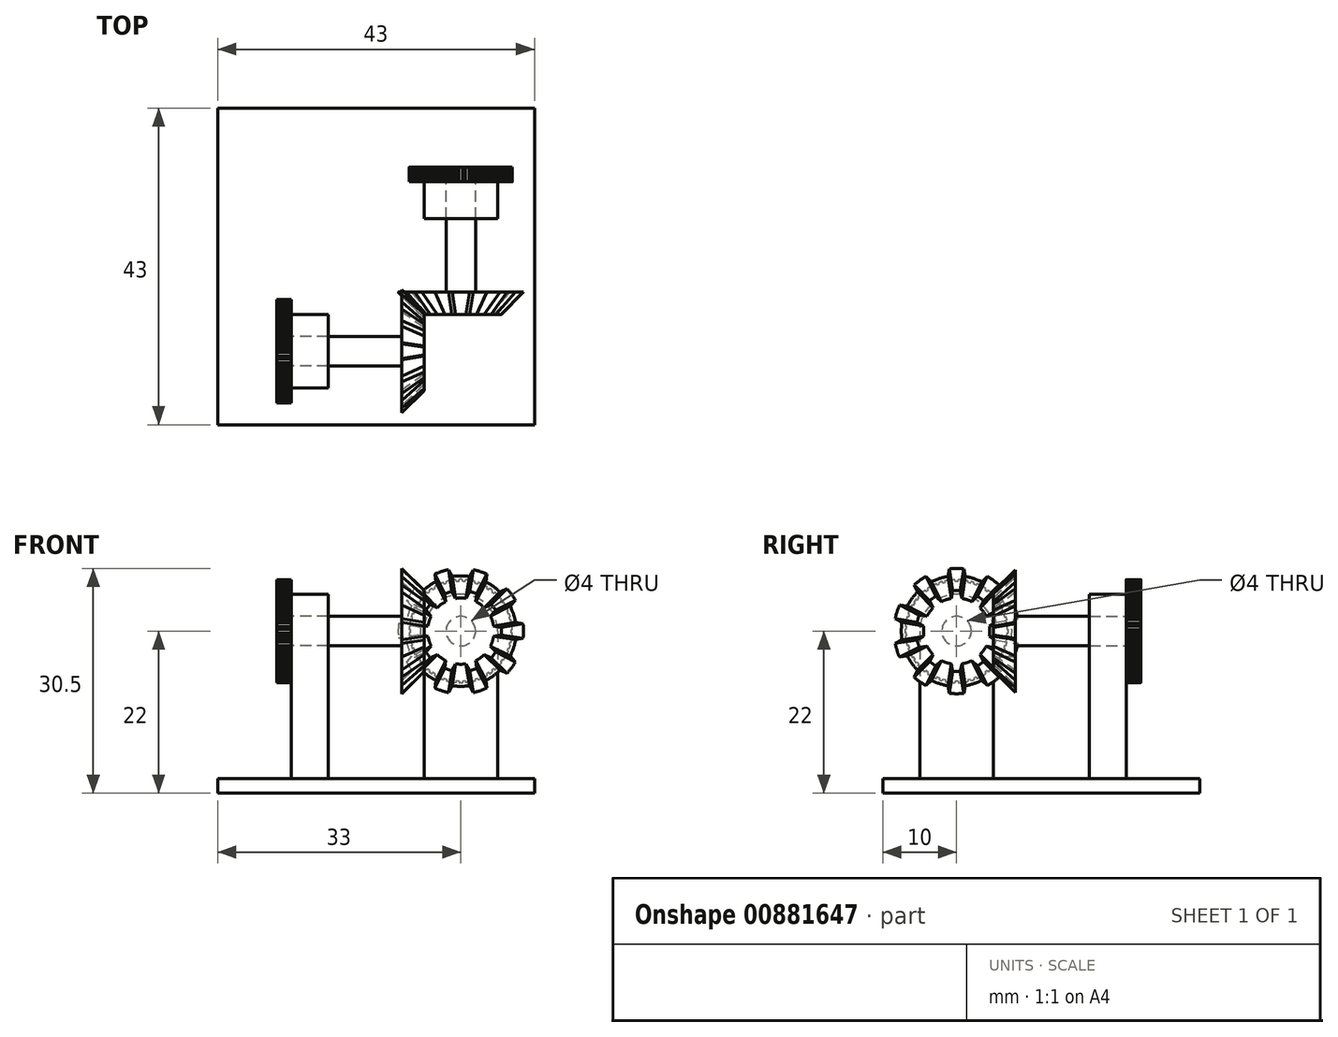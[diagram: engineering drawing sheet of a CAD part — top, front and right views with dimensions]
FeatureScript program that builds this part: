
annotation { "Feature Type Name" : "Feature", "Feature Type Description" : "" }
export const myFeature = defineFeature(function(context is Context, id is Id, definition is map)
    precondition{}
    {
        {
            var Q0;
            Q0=qCreatedBy(makeId("Top.planeOp"),FACE);
            var sketch = newSketch(context, id + "F0", { "sketchPlane" : qUnion([Q0])});
            skLineSegment(sketch, "E0", {"start": v(5, -5) * mm, "end": v(8, -8) * mm, "construction": true});
            skLineSegment(sketch, "E1", {"start": v(8, -8) * mm, "end": v(8, -2) * mm});
            skLineSegment(sketch, "E2", {"start": v(8, -2) * mm, "end": v(23, -2) * mm});
            skLineSegment(sketch, "E3", {"start": v(23, -2) * mm, "end": v(23, -7) * mm});
            skLineSegment(sketch, "E4", {"start": v(23, -7) * mm, "end": v(25, -7) * mm});
            skLineSegment(sketch, "E5", {"start": v(25, -7) * mm, "end": v(25, 0) * mm});
            skLineSegment(sketch, "E6", {"start": v(25, 0) * mm, "end": v(5, 0) * mm});
            skLineSegment(sketch, "E7", {"start": v(5, -5) * mm, "end": v(5, 0) * mm});
            skLineSegment(sketch, "E8", {"start": v(5, -5) * mm, "end": v(5, -5.5) * mm});
            skLineSegment(sketch, "E9", {"start": v(5, -5.5) * mm, "end": v(8, -8.5) * mm});
            skLineSegment(sketch, "E10", {"start": v(8, -8.5) * mm, "end": v(8, -8) * mm});
            skSolve(sketch);
        }
        {
            var Q0;
            Q0=makeQuery(id+"F0.imprint","IMPRINT",FACE,{"disambiguationData":[TD([[makeQuery(id+"F0.imprint","IMPRINT",EDGE,{"derivedFrom":sQuery(id+"F0.wireOp",EDGE,"E1")}),1.0]])]});
            var Q1;
            Q1=sQuery(id+"F0.wireOp",EDGE,"E6");
            revolve(context, id + "F1", {"surfaceOperationType" : NewSurfaceOperationType.NEW, "entities" : qUnion([Q0]), "axis" : qUnion([Q1]), "revolveType" : RevolveType.FULL});
        }
        {
            var Q0;
            Q0=makeQuery(id+"F1.opRevolve","SWEPT_FACE",FACE,{"disambiguationData":[OSD([sQuery(id+"F0.wireOp",EDGE,"E5")])]});
            var sketch = newSketch(context, id + "F2", { "sketchPlane" : qUnion([Q0])});
            skLineSegment(sketch, "E11", {"start": v(0.2, 7) * mm, "end": v(0.2, 6.8) * mm});
            skLineSegment(sketch, "E12", {"start": v(0.2, 6.8) * mm, "end": v(0, 6.8) * mm});
            skLineSegment(sketch, "E13.MirrorCS", {"start": v(-0.2, 6.8) * mm, "end": v(0, 6.8) * mm});
            skLineSegment(sketch, "E14.MirrorCS", {"start": v(-0.2, 7) * mm, "end": v(-0.2, 6.8) * mm});
            skArc(sketch, "E15", {"start": v(-0.2, 7) * mm, "mid": v(0, 7) * mm, "end": v(0.2, 7) * mm});
            skLineSegment(sketch, "E16.1.0", {"start": v(-1.08, 6.92) * mm, "end": v(-1.05, 6.72) * mm});
            skArc(sketch, "E16.1.1", {"start": v(-1.08, 6.92) * mm, "mid": v(-0.88, 6.94) * mm, "end": v(-0.68, 6.97) * mm});
            skLineSegment(sketch, "E16.1.2", {"start": v(-0.68, 6.97) * mm, "end": v(-0.65, 6.77) * mm});
            skLineSegment(sketch, "E16.1.3", {"start": v(-0.65, 6.77) * mm, "end": v(-0.85, 6.74) * mm});
            skLineSegment(sketch, "E16.1.4", {"start": v(-1.05, 6.72) * mm, "end": v(-0.85, 6.74) * mm});
            skLineSegment(sketch, "E16.2.0", {"start": v(-1.93, 6.73) * mm, "end": v(-1.88, 6.53) * mm});
            skArc(sketch, "E16.2.1", {"start": v(-1.93, 6.73) * mm, "mid": v(-1.74, 6.78) * mm, "end": v(-1.55, 6.83) * mm});
            skLineSegment(sketch, "E16.2.2", {"start": v(-1.55, 6.83) * mm, "end": v(-1.5, 6.63) * mm});
            skLineSegment(sketch, "E16.2.3", {"start": v(-1.5, 6.63) * mm, "end": v(-1.7, 6.58) * mm});
            skLineSegment(sketch, "E16.2.4", {"start": v(-1.88, 6.53) * mm, "end": v(-1.7, 6.58) * mm});
            skLineSegment(sketch, "E17.2.3.0", {"start": v(-2.76, 6.43) * mm, "end": v(-2.69, 6.25) * mm});
            skArc(sketch, "E17.3.3.0", {"start": v(-2.76, 6.43) * mm, "mid": v(-2.58, 6.5) * mm, "end": v(-2.39, 6.58) * mm});
            skLineSegment(sketch, "E17.7.3.0", {"start": v(-2.39, 6.58) * mm, "end": v(-2.32, 6.4) * mm});
            skLineSegment(sketch, "E17.10.3.0", {"start": v(-2.32, 6.4) * mm, "end": v(-2.5, 6.32) * mm});
            skLineSegment(sketch, "E17.13.3.0", {"start": v(-2.69, 6.25) * mm, "end": v(-2.5, 6.32) * mm});
            skLineSegment(sketch, "E17.2.4.0", {"start": v(-3.55, 6.04) * mm, "end": v(-3.45, 5.86) * mm});
            skArc(sketch, "E17.3.4.0", {"start": v(-3.55, 6.04) * mm, "mid": v(-3.37, 6.13) * mm, "end": v(-3.2, 6.23) * mm});
            skLineSegment(sketch, "E17.7.4.0", {"start": v(-3.2, 6.23) * mm, "end": v(-3.1, 6.05) * mm});
            skLineSegment(sketch, "E17.10.4.0", {"start": v(-3.1, 6.05) * mm, "end": v(-3.27, 5.96) * mm});
            skLineSegment(sketch, "E17.13.4.0", {"start": v(-3.45, 5.86) * mm, "end": v(-3.27, 5.96) * mm});
            skLineSegment(sketch, "E17.2.5.0", {"start": v(-4.27, 5.54) * mm, "end": v(-4.16, 5.38) * mm});
            skArc(sketch, "E17.3.5.0", {"start": v(-4.27, 5.54) * mm, "mid": v(-4.11, 5.66) * mm, "end": v(-3.95, 5.78) * mm});
            skLineSegment(sketch, "E17.7.5.0", {"start": v(-3.95, 5.78) * mm, "end": v(-3.83, 5.62) * mm});
            skLineSegment(sketch, "E17.10.5.0", {"start": v(-3.83, 5.62) * mm, "end": v(-4, 5.5) * mm});
            skLineSegment(sketch, "E17.13.5.0", {"start": v(-4.16, 5.38) * mm, "end": v(-4, 5.5) * mm});
            skLineSegment(sketch, "E17.2.6.0", {"start": v(-4.94, 4.96) * mm, "end": v(-4.8, 4.82) * mm});
            skArc(sketch, "E17.3.6.0", {"start": v(-4.94, 4.96) * mm, "mid": v(-4.8, 5.1) * mm, "end": v(-4.64, 5.24) * mm});
            skLineSegment(sketch, "E17.7.6.0", {"start": v(-4.64, 5.24) * mm, "end": v(-4.5, 5.1) * mm});
            skLineSegment(sketch, "E17.10.6.0", {"start": v(-4.5, 5.1) * mm, "end": v(-4.65, 4.95) * mm});
            skLineSegment(sketch, "E17.13.6.0", {"start": v(-4.8, 4.82) * mm, "end": v(-4.65, 4.95) * mm});
            skLineSegment(sketch, "E17.2.7.0", {"start": v(-5.52, 4.3) * mm, "end": v(-5.36, 4.18) * mm});
            skArc(sketch, "E17.3.7.0", {"start": v(-5.52, 4.3) * mm, "mid": v(-5.4, 4.46) * mm, "end": v(-5.26, 4.61) * mm});
            skLineSegment(sketch, "E17.7.7.0", {"start": v(-5.26, 4.61) * mm, "end": v(-5.1, 4.49) * mm});
            skLineSegment(sketch, "E17.10.7.0", {"start": v(-5.1, 4.49) * mm, "end": v(-5.24, 4.33) * mm});
            skLineSegment(sketch, "E17.13.7.0", {"start": v(-5.36, 4.18) * mm, "end": v(-5.24, 4.33) * mm});
            skLineSegment(sketch, "E17.2.8.0", {"start": v(-6.02, 3.58) * mm, "end": v(-5.85, 3.47) * mm});
            skArc(sketch, "E17.3.8.0", {"start": v(-6.02, 3.58) * mm, "mid": v(-5.91, 3.75) * mm, "end": v(-5.8, 3.92) * mm});
            skLineSegment(sketch, "E17.7.8.0", {"start": v(-5.8, 3.92) * mm, "end": v(-5.63, 3.81) * mm});
            skLineSegment(sketch, "E17.10.8.0", {"start": v(-5.63, 3.81) * mm, "end": v(-5.74, 3.64) * mm});
            skLineSegment(sketch, "E17.13.8.0", {"start": v(-5.85, 3.47) * mm, "end": v(-5.74, 3.64) * mm});
            skLineSegment(sketch, "E17.2.9.0", {"start": v(-6.42, 2.8) * mm, "end": v(-6.24, 2.71) * mm});
            skArc(sketch, "E17.3.9.0", {"start": v(-6.42, 2.8) * mm, "mid": v(-6.33, 2.98) * mm, "end": v(-6.25, 3.16) * mm});
            skLineSegment(sketch, "E17.7.9.0", {"start": v(-6.25, 3.16) * mm, "end": v(-6.07, 3.08) * mm});
            skLineSegment(sketch, "E17.10.9.0", {"start": v(-6.07, 3.08) * mm, "end": v(-6.15, 2.9) * mm});
            skLineSegment(sketch, "E17.13.9.0", {"start": v(-6.24, 2.71) * mm, "end": v(-6.15, 2.9) * mm});
            skLineSegment(sketch, "E17.2.10.0", {"start": v(-6.72, 1.97) * mm, "end": v(-6.53, 1.91) * mm});
            skArc(sketch, "E17.3.10.0", {"start": v(-6.72, 1.97) * mm, "mid": v(-6.66, 2.16) * mm, "end": v(-6.6, 2.35) * mm});
            skLineSegment(sketch, "E17.7.10.0", {"start": v(-6.6, 2.35) * mm, "end": v(-6.4, 2.3) * mm});
            skLineSegment(sketch, "E17.10.10.0", {"start": v(-6.4, 2.3) * mm, "end": v(-6.46, 2.1) * mm});
            skLineSegment(sketch, "E17.13.10.0", {"start": v(-6.53, 1.91) * mm, "end": v(-6.46, 2.1) * mm});
            skLineSegment(sketch, "E17.2.11.0", {"start": v(-6.91, 1.11) * mm, "end": v(-6.71, 1.08) * mm});
            skArc(sketch, "E17.3.11.0", {"start": v(-6.91, 1.11) * mm, "mid": v(-6.88, 1.31) * mm, "end": v(-6.84, 1.5) * mm});
            skLineSegment(sketch, "E17.7.11.0", {"start": v(-6.84, 1.5) * mm, "end": v(-6.64, 1.47) * mm});
            skLineSegment(sketch, "E17.10.11.0", {"start": v(-6.64, 1.47) * mm, "end": v(-6.68, 1.27) * mm});
            skLineSegment(sketch, "E17.13.11.0", {"start": v(-6.71, 1.08) * mm, "end": v(-6.68, 1.27) * mm});
            skLineSegment(sketch, "E17.2.12.0", {"start": v(-7, 0.24) * mm, "end": v(-6.8, 0.23) * mm});
            skArc(sketch, "E17.3.12.0", {"start": v(-7, 0.24) * mm, "mid": v(-6.99, 0.44) * mm, "end": v(-6.97, 0.64) * mm});
            skLineSegment(sketch, "E17.7.12.0", {"start": v(-6.97, 0.64) * mm, "end": v(-6.77, 0.63) * mm});
            skLineSegment(sketch, "E17.10.12.0", {"start": v(-6.77, 0.63) * mm, "end": v(-6.78, 0.43) * mm});
            skLineSegment(sketch, "E17.13.12.0", {"start": v(-6.8, 0.23) * mm, "end": v(-6.78, 0.43) * mm});
            skLineSegment(sketch, "E17.2.13.0", {"start": v(-6.97, -0.64) * mm, "end": v(-6.77, -0.63) * mm});
            skArc(sketch, "E17.3.13.0", {"start": v(-6.97, -0.64) * mm, "mid": v(-6.99, -0.44) * mm, "end": v(-7, -0.24) * mm});
            skLineSegment(sketch, "E17.7.13.0", {"start": v(-7, -0.24) * mm, "end": v(-6.8, -0.23) * mm});
            skLineSegment(sketch, "E17.10.13.0", {"start": v(-6.8, -0.23) * mm, "end": v(-6.78, -0.43) * mm});
            skLineSegment(sketch, "E17.13.13.0", {"start": v(-6.77, -0.63) * mm, "end": v(-6.78, -0.43) * mm});
            skLineSegment(sketch, "E17.2.14.0", {"start": v(-6.84, -1.5) * mm, "end": v(-6.64, -1.47) * mm});
            skArc(sketch, "E17.3.14.0", {"start": v(-6.84, -1.5) * mm, "mid": v(-6.88, -1.31) * mm, "end": v(-6.91, -1.11) * mm});
            skLineSegment(sketch, "E17.7.14.0", {"start": v(-6.91, -1.11) * mm, "end": v(-6.71, -1.08) * mm});
            skLineSegment(sketch, "E17.10.14.0", {"start": v(-6.71, -1.08) * mm, "end": v(-6.68, -1.27) * mm});
            skLineSegment(sketch, "E17.13.14.0", {"start": v(-6.64, -1.47) * mm, "end": v(-6.68, -1.27) * mm});
            skLineSegment(sketch, "E17.2.15.0", {"start": v(-6.6, -2.35) * mm, "end": v(-6.4, -2.3) * mm});
            skArc(sketch, "E17.3.15.0", {"start": v(-6.6, -2.35) * mm, "mid": v(-6.66, -2.16) * mm, "end": v(-6.72, -1.97) * mm});
            skLineSegment(sketch, "E17.7.15.0", {"start": v(-6.72, -1.97) * mm, "end": v(-6.53, -1.91) * mm});
            skLineSegment(sketch, "E17.10.15.0", {"start": v(-6.53, -1.91) * mm, "end": v(-6.46, -2.1) * mm});
            skLineSegment(sketch, "E17.13.15.0", {"start": v(-6.4, -2.3) * mm, "end": v(-6.46, -2.1) * mm});
            skLineSegment(sketch, "E17.2.16.0", {"start": v(-6.25, -3.16) * mm, "end": v(-6.07, -3.08) * mm});
            skArc(sketch, "E17.3.16.0", {"start": v(-6.25, -3.16) * mm, "mid": v(-6.33, -2.98) * mm, "end": v(-6.42, -2.8) * mm});
            skLineSegment(sketch, "E17.7.16.0", {"start": v(-6.42, -2.8) * mm, "end": v(-6.24, -2.71) * mm});
            skLineSegment(sketch, "E17.10.16.0", {"start": v(-6.24, -2.71) * mm, "end": v(-6.15, -2.9) * mm});
            skLineSegment(sketch, "E17.13.16.0", {"start": v(-6.07, -3.08) * mm, "end": v(-6.15, -2.9) * mm});
            skLineSegment(sketch, "E17.2.17.0", {"start": v(-5.8, -3.92) * mm, "end": v(-5.63, -3.81) * mm});
            skArc(sketch, "E17.3.17.0", {"start": v(-5.8, -3.92) * mm, "mid": v(-5.91, -3.75) * mm, "end": v(-6.02, -3.58) * mm});
            skLineSegment(sketch, "E17.7.17.0", {"start": v(-6.02, -3.58) * mm, "end": v(-5.85, -3.47) * mm});
            skLineSegment(sketch, "E17.10.17.0", {"start": v(-5.85, -3.47) * mm, "end": v(-5.74, -3.64) * mm});
            skLineSegment(sketch, "E17.13.17.0", {"start": v(-5.63, -3.81) * mm, "end": v(-5.74, -3.64) * mm});
            skLineSegment(sketch, "E17.2.18.0", {"start": v(-5.26, -4.61) * mm, "end": v(-5.1, -4.49) * mm});
            skArc(sketch, "E17.3.18.0", {"start": v(-5.26, -4.61) * mm, "mid": v(-5.4, -4.46) * mm, "end": v(-5.52, -4.3) * mm});
            skLineSegment(sketch, "E17.7.18.0", {"start": v(-5.52, -4.3) * mm, "end": v(-5.36, -4.18) * mm});
            skLineSegment(sketch, "E17.10.18.0", {"start": v(-5.36, -4.18) * mm, "end": v(-5.24, -4.33) * mm});
            skLineSegment(sketch, "E17.13.18.0", {"start": v(-5.1, -4.49) * mm, "end": v(-5.24, -4.33) * mm});
            skLineSegment(sketch, "E17.2.19.0", {"start": v(-4.64, -5.24) * mm, "end": v(-4.5, -5.1) * mm});
            skArc(sketch, "E17.3.19.0", {"start": v(-4.64, -5.24) * mm, "mid": v(-4.8, -5.1) * mm, "end": v(-4.94, -4.96) * mm});
            skLineSegment(sketch, "E17.7.19.0", {"start": v(-4.94, -4.96) * mm, "end": v(-4.8, -4.82) * mm});
            skLineSegment(sketch, "E17.10.19.0", {"start": v(-4.8, -4.82) * mm, "end": v(-4.65, -4.95) * mm});
            skLineSegment(sketch, "E17.13.19.0", {"start": v(-4.5, -5.1) * mm, "end": v(-4.65, -4.95) * mm});
            skLineSegment(sketch, "E17.2.20.0", {"start": v(-3.95, -5.78) * mm, "end": v(-3.83, -5.62) * mm});
            skArc(sketch, "E17.3.20.0", {"start": v(-3.95, -5.78) * mm, "mid": v(-4.11, -5.66) * mm, "end": v(-4.27, -5.54) * mm});
            skLineSegment(sketch, "E17.7.20.0", {"start": v(-4.27, -5.54) * mm, "end": v(-4.16, -5.38) * mm});
            skLineSegment(sketch, "E17.10.20.0", {"start": v(-4.16, -5.38) * mm, "end": v(-4, -5.5) * mm});
            skLineSegment(sketch, "E17.13.20.0", {"start": v(-3.83, -5.62) * mm, "end": v(-4, -5.5) * mm});
            skLineSegment(sketch, "E17.2.21.0", {"start": v(-3.2, -6.23) * mm, "end": v(-3.1, -6.05) * mm});
            skArc(sketch, "E17.3.21.0", {"start": v(-3.2, -6.23) * mm, "mid": v(-3.37, -6.13) * mm, "end": v(-3.55, -6.04) * mm});
            skLineSegment(sketch, "E17.7.21.0", {"start": v(-3.55, -6.04) * mm, "end": v(-3.45, -5.86) * mm});
            skLineSegment(sketch, "E17.10.21.0", {"start": v(-3.45, -5.86) * mm, "end": v(-3.27, -5.96) * mm});
            skLineSegment(sketch, "E17.13.21.0", {"start": v(-3.1, -6.05) * mm, "end": v(-3.27, -5.96) * mm});
            skLineSegment(sketch, "E17.2.22.0", {"start": v(-2.39, -6.58) * mm, "end": v(-2.32, -6.4) * mm});
            skArc(sketch, "E17.3.22.0", {"start": v(-2.39, -6.58) * mm, "mid": v(-2.58, -6.5) * mm, "end": v(-2.76, -6.43) * mm});
            skLineSegment(sketch, "E17.7.22.0", {"start": v(-2.76, -6.43) * mm, "end": v(-2.69, -6.25) * mm});
            skLineSegment(sketch, "E17.10.22.0", {"start": v(-2.69, -6.25) * mm, "end": v(-2.5, -6.32) * mm});
            skLineSegment(sketch, "E17.13.22.0", {"start": v(-2.32, -6.4) * mm, "end": v(-2.5, -6.32) * mm});
            skLineSegment(sketch, "E17.2.23.0", {"start": v(-1.55, -6.83) * mm, "end": v(-1.5, -6.63) * mm});
            skArc(sketch, "E17.3.23.0", {"start": v(-1.55, -6.83) * mm, "mid": v(-1.74, -6.78) * mm, "end": v(-1.93, -6.73) * mm});
            skLineSegment(sketch, "E17.7.23.0", {"start": v(-1.93, -6.73) * mm, "end": v(-1.88, -6.53) * mm});
            skLineSegment(sketch, "E17.10.23.0", {"start": v(-1.88, -6.53) * mm, "end": v(-1.7, -6.58) * mm});
            skLineSegment(sketch, "E17.13.23.0", {"start": v(-1.5, -6.63) * mm, "end": v(-1.7, -6.58) * mm});
            skLineSegment(sketch, "E17.2.24.0", {"start": v(-0.68, -6.97) * mm, "end": v(-0.65, -6.77) * mm});
            skArc(sketch, "E17.3.24.0", {"start": v(-0.68, -6.97) * mm, "mid": v(-0.88, -6.94) * mm, "end": v(-1.08, -6.92) * mm});
            skLineSegment(sketch, "E17.7.24.0", {"start": v(-1.08, -6.92) * mm, "end": v(-1.05, -6.72) * mm});
            skLineSegment(sketch, "E17.10.24.0", {"start": v(-1.05, -6.72) * mm, "end": v(-0.85, -6.74) * mm});
            skLineSegment(sketch, "E17.13.24.0", {"start": v(-0.65, -6.77) * mm, "end": v(-0.85, -6.74) * mm});
            skLineSegment(sketch, "E17.2.25.0", {"start": v(0.2, -7) * mm, "end": v(0.2, -6.8) * mm});
            skArc(sketch, "E17.3.25.0", {"start": v(0.2, -7) * mm, "mid": v(0, -7) * mm, "end": v(-0.2, -7) * mm});
            skLineSegment(sketch, "E17.7.25.0", {"start": v(-0.2, -7) * mm, "end": v(-0.2, -6.8) * mm});
            skLineSegment(sketch, "E17.10.25.0", {"start": v(-0.2, -6.8) * mm, "end": v(0, -6.8) * mm});
            skLineSegment(sketch, "E17.13.25.0", {"start": v(0.2, -6.8) * mm, "end": v(0, -6.8) * mm});
            skLineSegment(sketch, "E17.2.26.0", {"start": v(1.08, -6.92) * mm, "end": v(1.05, -6.72) * mm});
            skArc(sketch, "E17.3.26.0", {"start": v(1.08, -6.92) * mm, "mid": v(0.88, -6.94) * mm, "end": v(0.68, -6.97) * mm});
            skLineSegment(sketch, "E17.7.26.0", {"start": v(0.68, -6.97) * mm, "end": v(0.65, -6.77) * mm});
            skLineSegment(sketch, "E17.10.26.0", {"start": v(0.65, -6.77) * mm, "end": v(0.85, -6.74) * mm});
            skLineSegment(sketch, "E17.13.26.0", {"start": v(1.05, -6.72) * mm, "end": v(0.85, -6.74) * mm});
            skLineSegment(sketch, "E17.2.27.0", {"start": v(1.93, -6.73) * mm, "end": v(1.88, -6.53) * mm});
            skArc(sketch, "E17.3.27.0", {"start": v(1.93, -6.73) * mm, "mid": v(1.74, -6.78) * mm, "end": v(1.55, -6.83) * mm});
            skLineSegment(sketch, "E17.7.27.0", {"start": v(1.55, -6.83) * mm, "end": v(1.5, -6.63) * mm});
            skLineSegment(sketch, "E17.10.27.0", {"start": v(1.5, -6.63) * mm, "end": v(1.7, -6.58) * mm});
            skLineSegment(sketch, "E17.13.27.0", {"start": v(1.88, -6.53) * mm, "end": v(1.7, -6.58) * mm});
            skLineSegment(sketch, "E17.2.28.0", {"start": v(2.76, -6.43) * mm, "end": v(2.69, -6.25) * mm});
            skArc(sketch, "E17.3.28.0", {"start": v(2.76, -6.43) * mm, "mid": v(2.58, -6.5) * mm, "end": v(2.39, -6.58) * mm});
            skLineSegment(sketch, "E17.7.28.0", {"start": v(2.39, -6.58) * mm, "end": v(2.32, -6.4) * mm});
            skLineSegment(sketch, "E17.10.28.0", {"start": v(2.32, -6.4) * mm, "end": v(2.5, -6.32) * mm});
            skLineSegment(sketch, "E17.13.28.0", {"start": v(2.69, -6.25) * mm, "end": v(2.5, -6.32) * mm});
            skLineSegment(sketch, "E17.2.29.0", {"start": v(3.55, -6.04) * mm, "end": v(3.45, -5.86) * mm});
            skArc(sketch, "E17.3.29.0", {"start": v(3.55, -6.04) * mm, "mid": v(3.37, -6.13) * mm, "end": v(3.2, -6.23) * mm});
            skLineSegment(sketch, "E17.7.29.0", {"start": v(3.2, -6.23) * mm, "end": v(3.1, -6.05) * mm});
            skLineSegment(sketch, "E17.10.29.0", {"start": v(3.1, -6.05) * mm, "end": v(3.27, -5.96) * mm});
            skLineSegment(sketch, "E17.13.29.0", {"start": v(3.45, -5.86) * mm, "end": v(3.27, -5.96) * mm});
            skLineSegment(sketch, "E17.2.30.0", {"start": v(4.27, -5.54) * mm, "end": v(4.16, -5.38) * mm});
            skArc(sketch, "E17.3.30.0", {"start": v(4.27, -5.54) * mm, "mid": v(4.11, -5.66) * mm, "end": v(3.95, -5.78) * mm});
            skLineSegment(sketch, "E17.7.30.0", {"start": v(3.95, -5.78) * mm, "end": v(3.83, -5.62) * mm});
            skLineSegment(sketch, "E17.10.30.0", {"start": v(3.83, -5.62) * mm, "end": v(4, -5.5) * mm});
            skLineSegment(sketch, "E17.13.30.0", {"start": v(4.16, -5.38) * mm, "end": v(4, -5.5) * mm});
            skLineSegment(sketch, "E17.2.31.0", {"start": v(4.94, -4.96) * mm, "end": v(4.8, -4.82) * mm});
            skArc(sketch, "E17.3.31.0", {"start": v(4.94, -4.96) * mm, "mid": v(4.8, -5.1) * mm, "end": v(4.64, -5.24) * mm});
            skLineSegment(sketch, "E17.7.31.0", {"start": v(4.64, -5.24) * mm, "end": v(4.5, -5.1) * mm});
            skLineSegment(sketch, "E17.10.31.0", {"start": v(4.5, -5.1) * mm, "end": v(4.65, -4.95) * mm});
            skLineSegment(sketch, "E17.13.31.0", {"start": v(4.8, -4.82) * mm, "end": v(4.65, -4.95) * mm});
            skLineSegment(sketch, "E17.2.32.0", {"start": v(5.52, -4.3) * mm, "end": v(5.36, -4.18) * mm});
            skArc(sketch, "E17.3.32.0", {"start": v(5.52, -4.3) * mm, "mid": v(5.4, -4.46) * mm, "end": v(5.26, -4.61) * mm});
            skLineSegment(sketch, "E17.7.32.0", {"start": v(5.26, -4.61) * mm, "end": v(5.1, -4.49) * mm});
            skLineSegment(sketch, "E17.10.32.0", {"start": v(5.1, -4.49) * mm, "end": v(5.24, -4.33) * mm});
            skLineSegment(sketch, "E17.13.32.0", {"start": v(5.36, -4.18) * mm, "end": v(5.24, -4.33) * mm});
            skLineSegment(sketch, "E17.2.33.0", {"start": v(6.02, -3.58) * mm, "end": v(5.85, -3.47) * mm});
            skArc(sketch, "E17.3.33.0", {"start": v(6.02, -3.58) * mm, "mid": v(5.91, -3.75) * mm, "end": v(5.8, -3.92) * mm});
            skLineSegment(sketch, "E17.7.33.0", {"start": v(5.8, -3.92) * mm, "end": v(5.63, -3.81) * mm});
            skLineSegment(sketch, "E17.10.33.0", {"start": v(5.63, -3.81) * mm, "end": v(5.74, -3.64) * mm});
            skLineSegment(sketch, "E17.13.33.0", {"start": v(5.85, -3.47) * mm, "end": v(5.74, -3.64) * mm});
            skLineSegment(sketch, "E17.2.34.0", {"start": v(6.42, -2.8) * mm, "end": v(6.24, -2.71) * mm});
            skArc(sketch, "E17.3.34.0", {"start": v(6.42, -2.8) * mm, "mid": v(6.33, -2.98) * mm, "end": v(6.25, -3.16) * mm});
            skLineSegment(sketch, "E17.7.34.0", {"start": v(6.25, -3.16) * mm, "end": v(6.07, -3.08) * mm});
            skLineSegment(sketch, "E17.10.34.0", {"start": v(6.07, -3.08) * mm, "end": v(6.15, -2.9) * mm});
            skLineSegment(sketch, "E17.13.34.0", {"start": v(6.24, -2.71) * mm, "end": v(6.15, -2.9) * mm});
            skLineSegment(sketch, "E17.2.35.0", {"start": v(6.72, -1.97) * mm, "end": v(6.53, -1.91) * mm});
            skArc(sketch, "E17.3.35.0", {"start": v(6.72, -1.97) * mm, "mid": v(6.66, -2.16) * mm, "end": v(6.6, -2.35) * mm});
            skLineSegment(sketch, "E17.7.35.0", {"start": v(6.6, -2.35) * mm, "end": v(6.4, -2.3) * mm});
            skLineSegment(sketch, "E17.10.35.0", {"start": v(6.4, -2.3) * mm, "end": v(6.46, -2.1) * mm});
            skLineSegment(sketch, "E17.13.35.0", {"start": v(6.53, -1.91) * mm, "end": v(6.46, -2.1) * mm});
            skLineSegment(sketch, "E17.2.36.0", {"start": v(6.91, -1.11) * mm, "end": v(6.71, -1.08) * mm});
            skArc(sketch, "E17.3.36.0", {"start": v(6.91, -1.11) * mm, "mid": v(6.88, -1.31) * mm, "end": v(6.84, -1.5) * mm});
            skLineSegment(sketch, "E17.7.36.0", {"start": v(6.84, -1.5) * mm, "end": v(6.64, -1.47) * mm});
            skLineSegment(sketch, "E17.10.36.0", {"start": v(6.64, -1.47) * mm, "end": v(6.68, -1.27) * mm});
            skLineSegment(sketch, "E17.13.36.0", {"start": v(6.71, -1.08) * mm, "end": v(6.68, -1.27) * mm});
            skLineSegment(sketch, "E17.2.37.0", {"start": v(7, -0.24) * mm, "end": v(6.8, -0.23) * mm});
            skArc(sketch, "E17.3.37.0", {"start": v(7, -0.24) * mm, "mid": v(6.99, -0.44) * mm, "end": v(6.97, -0.64) * mm});
            skLineSegment(sketch, "E17.7.37.0", {"start": v(6.97, -0.64) * mm, "end": v(6.77, -0.63) * mm});
            skLineSegment(sketch, "E17.10.37.0", {"start": v(6.77, -0.63) * mm, "end": v(6.78, -0.43) * mm});
            skLineSegment(sketch, "E17.13.37.0", {"start": v(6.8, -0.23) * mm, "end": v(6.78, -0.43) * mm});
            skLineSegment(sketch, "E17.2.38.0", {"start": v(6.97, 0.64) * mm, "end": v(6.77, 0.63) * mm});
            skArc(sketch, "E17.3.38.0", {"start": v(6.97, 0.64) * mm, "mid": v(6.99, 0.44) * mm, "end": v(7, 0.24) * mm});
            skLineSegment(sketch, "E17.7.38.0", {"start": v(7, 0.24) * mm, "end": v(6.8, 0.23) * mm});
            skLineSegment(sketch, "E17.10.38.0", {"start": v(6.8, 0.23) * mm, "end": v(6.78, 0.43) * mm});
            skLineSegment(sketch, "E17.13.38.0", {"start": v(6.77, 0.63) * mm, "end": v(6.78, 0.43) * mm});
            skLineSegment(sketch, "E17.2.39.0", {"start": v(6.84, 1.5) * mm, "end": v(6.64, 1.47) * mm});
            skArc(sketch, "E17.3.39.0", {"start": v(6.84, 1.5) * mm, "mid": v(6.88, 1.31) * mm, "end": v(6.91, 1.11) * mm});
            skLineSegment(sketch, "E17.7.39.0", {"start": v(6.91, 1.11) * mm, "end": v(6.71, 1.08) * mm});
            skLineSegment(sketch, "E17.10.39.0", {"start": v(6.71, 1.08) * mm, "end": v(6.68, 1.27) * mm});
            skLineSegment(sketch, "E17.13.39.0", {"start": v(6.64, 1.47) * mm, "end": v(6.68, 1.27) * mm});
            skLineSegment(sketch, "E17.2.40.0", {"start": v(6.6, 2.35) * mm, "end": v(6.4, 2.3) * mm});
            skArc(sketch, "E17.3.40.0", {"start": v(6.6, 2.35) * mm, "mid": v(6.66, 2.16) * mm, "end": v(6.72, 1.97) * mm});
            skLineSegment(sketch, "E17.7.40.0", {"start": v(6.72, 1.97) * mm, "end": v(6.53, 1.91) * mm});
            skLineSegment(sketch, "E17.10.40.0", {"start": v(6.53, 1.91) * mm, "end": v(6.46, 2.1) * mm});
            skLineSegment(sketch, "E17.13.40.0", {"start": v(6.4, 2.3) * mm, "end": v(6.46, 2.1) * mm});
            skLineSegment(sketch, "E17.2.41.0", {"start": v(6.25, 3.16) * mm, "end": v(6.07, 3.08) * mm});
            skArc(sketch, "E17.3.41.0", {"start": v(6.25, 3.16) * mm, "mid": v(6.33, 2.98) * mm, "end": v(6.42, 2.8) * mm});
            skLineSegment(sketch, "E17.7.41.0", {"start": v(6.42, 2.8) * mm, "end": v(6.24, 2.71) * mm});
            skLineSegment(sketch, "E17.10.41.0", {"start": v(6.24, 2.71) * mm, "end": v(6.15, 2.9) * mm});
            skLineSegment(sketch, "E17.13.41.0", {"start": v(6.07, 3.08) * mm, "end": v(6.15, 2.9) * mm});
            skLineSegment(sketch, "E17.2.42.0", {"start": v(5.8, 3.92) * mm, "end": v(5.63, 3.81) * mm});
            skArc(sketch, "E17.3.42.0", {"start": v(5.8, 3.92) * mm, "mid": v(5.91, 3.75) * mm, "end": v(6.02, 3.58) * mm});
            skLineSegment(sketch, "E17.7.42.0", {"start": v(6.02, 3.58) * mm, "end": v(5.85, 3.47) * mm});
            skLineSegment(sketch, "E17.10.42.0", {"start": v(5.85, 3.47) * mm, "end": v(5.74, 3.64) * mm});
            skLineSegment(sketch, "E17.13.42.0", {"start": v(5.63, 3.81) * mm, "end": v(5.74, 3.64) * mm});
            skLineSegment(sketch, "E17.2.43.0", {"start": v(5.26, 4.61) * mm, "end": v(5.1, 4.49) * mm});
            skArc(sketch, "E17.3.43.0", {"start": v(5.26, 4.61) * mm, "mid": v(5.4, 4.46) * mm, "end": v(5.52, 4.3) * mm});
            skLineSegment(sketch, "E17.7.43.0", {"start": v(5.52, 4.3) * mm, "end": v(5.36, 4.18) * mm});
            skLineSegment(sketch, "E17.10.43.0", {"start": v(5.36, 4.18) * mm, "end": v(5.24, 4.33) * mm});
            skLineSegment(sketch, "E17.13.43.0", {"start": v(5.1, 4.49) * mm, "end": v(5.24, 4.33) * mm});
            skLineSegment(sketch, "E17.2.44.0", {"start": v(4.64, 5.24) * mm, "end": v(4.5, 5.1) * mm});
            skArc(sketch, "E17.3.44.0", {"start": v(4.64, 5.24) * mm, "mid": v(4.8, 5.1) * mm, "end": v(4.94, 4.96) * mm});
            skLineSegment(sketch, "E17.7.44.0", {"start": v(4.94, 4.96) * mm, "end": v(4.8, 4.82) * mm});
            skLineSegment(sketch, "E17.10.44.0", {"start": v(4.8, 4.82) * mm, "end": v(4.65, 4.95) * mm});
            skLineSegment(sketch, "E17.13.44.0", {"start": v(4.5, 5.1) * mm, "end": v(4.65, 4.95) * mm});
            skLineSegment(sketch, "E17.2.45.0", {"start": v(3.95, 5.78) * mm, "end": v(3.83, 5.62) * mm});
            skArc(sketch, "E17.3.45.0", {"start": v(3.95, 5.78) * mm, "mid": v(4.11, 5.66) * mm, "end": v(4.27, 5.54) * mm});
            skLineSegment(sketch, "E17.7.45.0", {"start": v(4.27, 5.54) * mm, "end": v(4.16, 5.38) * mm});
            skLineSegment(sketch, "E17.10.45.0", {"start": v(4.16, 5.38) * mm, "end": v(4, 5.5) * mm});
            skLineSegment(sketch, "E17.13.45.0", {"start": v(3.83, 5.62) * mm, "end": v(4, 5.5) * mm});
            skLineSegment(sketch, "E17.2.46.0", {"start": v(3.2, 6.23) * mm, "end": v(3.1, 6.05) * mm});
            skArc(sketch, "E17.3.46.0", {"start": v(3.2, 6.23) * mm, "mid": v(3.37, 6.13) * mm, "end": v(3.55, 6.04) * mm});
            skLineSegment(sketch, "E17.7.46.0", {"start": v(3.55, 6.04) * mm, "end": v(3.45, 5.86) * mm});
            skLineSegment(sketch, "E17.10.46.0", {"start": v(3.45, 5.86) * mm, "end": v(3.27, 5.96) * mm});
            skLineSegment(sketch, "E17.13.46.0", {"start": v(3.1, 6.05) * mm, "end": v(3.27, 5.96) * mm});
            skLineSegment(sketch, "E17.2.47.0", {"start": v(2.39, 6.58) * mm, "end": v(2.32, 6.4) * mm});
            skArc(sketch, "E17.3.47.0", {"start": v(2.39, 6.58) * mm, "mid": v(2.58, 6.5) * mm, "end": v(2.76, 6.43) * mm});
            skLineSegment(sketch, "E17.7.47.0", {"start": v(2.76, 6.43) * mm, "end": v(2.69, 6.25) * mm});
            skLineSegment(sketch, "E17.10.47.0", {"start": v(2.69, 6.25) * mm, "end": v(2.5, 6.32) * mm});
            skLineSegment(sketch, "E17.13.47.0", {"start": v(2.32, 6.4) * mm, "end": v(2.5, 6.32) * mm});
            skLineSegment(sketch, "E17.2.48.0", {"start": v(1.55, 6.83) * mm, "end": v(1.5, 6.63) * mm});
            skArc(sketch, "E17.3.48.0", {"start": v(1.55, 6.83) * mm, "mid": v(1.74, 6.78) * mm, "end": v(1.93, 6.73) * mm});
            skLineSegment(sketch, "E17.7.48.0", {"start": v(1.93, 6.73) * mm, "end": v(1.88, 6.53) * mm});
            skLineSegment(sketch, "E17.10.48.0", {"start": v(1.88, 6.53) * mm, "end": v(1.7, 6.58) * mm});
            skLineSegment(sketch, "E17.13.48.0", {"start": v(1.5, 6.63) * mm, "end": v(1.7, 6.58) * mm});
            skLineSegment(sketch, "E17.2.49.0", {"start": v(0.68, 6.97) * mm, "end": v(0.65, 6.77) * mm});
            skArc(sketch, "E17.3.49.0", {"start": v(0.68, 6.97) * mm, "mid": v(0.88, 6.94) * mm, "end": v(1.08, 6.92) * mm});
            skLineSegment(sketch, "E17.7.49.0", {"start": v(1.08, 6.92) * mm, "end": v(1.05, 6.72) * mm});
            skLineSegment(sketch, "E17.10.49.0", {"start": v(1.05, 6.72) * mm, "end": v(0.85, 6.74) * mm});
            skLineSegment(sketch, "E17.13.49.0", {"start": v(0.65, 6.77) * mm, "end": v(0.85, 6.74) * mm});
            skSolve(sketch);
        }
        {
            var Q0;
            Q0 = qSketchRegion(id + "F2", true);
            var Q1;
            Q1=makeQuery(id+"F1.opRevolve","SWEPT_FACE",FACE,{"disambiguationData":[OSD([sQuery(id+"F0.wireOp",EDGE,"E3")])]});
            extrude(context, id + "F3", {"entities" : qUnion([Q0]), "operationType" : NewBodyOperationType.REMOVE, "endBound" : BoundingType.UP_TO_SURFACE, "oppositeDirection" : true, "depth" : 25 * mm, "endBoundEntityFace" : qUnion([Q1]), "offsetDistance" : 25 * mm});
        }
        {
            var Q0;
            Q0=makeQuery(id+"F1.opRevolve","SWEPT_FACE",FACE,{"disambiguationData":[OSD([sQuery(id+"F0.wireOp",EDGE,"E7"),sQuery(id+"F0.wireOp",EDGE,"E8")])]});
            var sketch = newSketch(context, id + "F4", { "sketchPlane" : qUnion([Q0])});
            skLineSegment(sketch, "E18", {"start": v(5.43, 0.86) * mm, "end": v(4.44, 0.7) * mm, "construction": true});
            skArc(sketch, "E19", {"start": v(4.44, 0.7) * mm, "mid": v(4.5, 0) * mm, "end": v(4.44, -0.7) * mm});
            skLineSegment(sketch, "E20.MirrorCS", {"start": v(5.43, -0.86) * mm, "end": v(4.44, -0.7) * mm, "construction": true});
            skLineSegment(sketch, "E21", {"start": v(4.44, 0.7) * mm, "end": v(5.36, 1.21) * mm});
            skLineSegment(sketch, "E22.MirrorCS", {"start": v(4.44, -0.7) * mm, "end": v(5.36, -1.21) * mm});
            skArc(sketch, "E23", {"start": v(5.36, 1.21) * mm, "mid": v(5.5, 0) * mm, "end": v(5.36, -1.21) * mm});
            skSolve(sketch);
        }
        {
            var Q0;
            Q0=makeQuery(id+"F1.opRevolve","SWEPT_FACE",FACE,{"disambiguationData":[OSD([sQuery(id+"F0.wireOp",EDGE,"E1"),sQuery(id+"F0.wireOp",EDGE,"E10")])]});
            var sketch = newSketch(context, id + "F5", { "sketchPlane" : qUnion([Q0])});
            skArc(sketch, "E24.0", {"start": v(-7.4, 1.17) * mm, "mid": v(-7.5, 0) * mm, "end": v(-7.4, -1.17) * mm});
            skLineSegment(sketch, "E25", {"start": v(-8.4, 1.33) * mm, "end": v(-7.4, 1.17) * mm, "construction": true});
            skLineSegment(sketch, "E26.MirrorCS", {"start": v(-8.4, -1.33) * mm, "end": v(-7.4, -1.17) * mm, "construction": true});
            skLineSegment(sketch, "E27", {"start": v(-7.4, 1.17) * mm, "end": v(-8.33, 1.69) * mm});
            skLineSegment(sketch, "E28.MirrorCS", {"start": v(-7.4, -1.17) * mm, "end": v(-8.33, -1.69) * mm});
            skArc(sketch, "E29", {"start": v(-8.33, 1.69) * mm, "mid": v(-8.5, 0) * mm, "end": v(-8.33, -1.69) * mm});
            skSolve(sketch);
        }
        {
            var Q1;
            Q1 = qSketchRegion(id + "F4", true);
            var Q2;
            Q2 = qSketchRegion(id + "F5", true);
            loft(context, id + "F6", {"sheetProfilesArray" : [{ "sheetProfileEntities" : qUnion([Q1]) }, { "sheetProfileEntities" : qUnion([Q2]) }]});
        }
        {
            var Q0;
            Q0=makeQuery(id+"F6.opLoft","SWEPT_BODY",BODY,{"disambiguationData":[OSD([makeQuery(id+"F4.imprint","IMPRINT",FACE,{"disambiguationData":[TD([[makeQuery(id+"F4.imprint","IMPRINT",EDGE,{"derivedFrom":sQuery(id+"F4.wireOp",EDGE,"E19")}),1.0]])]}),makeQuery(id+"F5.imprint","IMPRINT",FACE,{"disambiguationData":[TD([[makeQuery(id+"F5.imprint","IMPRINT",EDGE,{"derivedFrom":sQuery(id+"F5.wireOp",EDGE,"E24.0")}),-1.0]])]})])]});
            var Q1;
            Q1=makeQuery(id+"F1.opRevolve","SWEPT_EDGE",EDGE,{"disambiguationData":[OSD([sQuery(id+"F0.wireOp",EDGE,"E8"),sQuery(id+"F0.wireOp",EDGE,"E9")])]});
            circularPattern(context, id + "F7", {"entities" : qUnion([Q0]), "axis" : qUnion([Q1]), "angle" : 360 * degree, "instanceCount" : 10, "equalSpace" : true});
        }
        {
            var Q0;
            Q0=makeQuery(id+"F6.opLoft","SWEPT_BODY",BODY,{"disambiguationData":[OSD([makeQuery(id+"F4.imprint","IMPRINT",FACE,{"disambiguationData":[TD([[makeQuery(id+"F4.imprint","IMPRINT",EDGE,{"derivedFrom":sQuery(id+"F4.wireOp",EDGE,"E19")}),1.0]])]}),makeQuery(id+"F5.imprint","IMPRINT",FACE,{"disambiguationData":[TD([[makeQuery(id+"F5.imprint","IMPRINT",EDGE,{"derivedFrom":sQuery(id+"F5.wireOp",EDGE,"E24.0")}),-1.0]])]})])]});
            var Q1;
            Q1=makeQuery(id+"F7.opPattern","COPY",BODY,{"derivedFrom":makeQuery(id+"F6.opLoft","SWEPT_BODY",BODY,{"disambiguationData":[OSD([makeQuery(id+"F4.imprint","IMPRINT",FACE,{"disambiguationData":[TD([[makeQuery(id+"F4.imprint","IMPRINT",EDGE,{"derivedFrom":sQuery(id+"F4.wireOp",EDGE,"E19")}),1.0]])]}),makeQuery(id+"F5.imprint","IMPRINT",FACE,{"disambiguationData":[TD([[makeQuery(id+"F5.imprint","IMPRINT",EDGE,{"derivedFrom":sQuery(id+"F5.wireOp",EDGE,"E24.0")}),-1.0]])]})])]}),"instanceName":"2"});
            var Q2;
            Q2=makeQuery(id+"F7.opPattern","COPY",BODY,{"derivedFrom":makeQuery(id+"F6.opLoft","SWEPT_BODY",BODY,{"disambiguationData":[OSD([makeQuery(id+"F4.imprint","IMPRINT",FACE,{"disambiguationData":[TD([[makeQuery(id+"F4.imprint","IMPRINT",EDGE,{"derivedFrom":sQuery(id+"F4.wireOp",EDGE,"E19")}),1.0]])]}),makeQuery(id+"F5.imprint","IMPRINT",FACE,{"disambiguationData":[TD([[makeQuery(id+"F5.imprint","IMPRINT",EDGE,{"derivedFrom":sQuery(id+"F5.wireOp",EDGE,"E24.0")}),-1.0]])]})])]}),"instanceName":"4"});
            var Q3;
            Q3=makeQuery(id+"F7.opPattern","COPY",BODY,{"derivedFrom":makeQuery(id+"F6.opLoft","SWEPT_BODY",BODY,{"disambiguationData":[OSD([makeQuery(id+"F4.imprint","IMPRINT",FACE,{"disambiguationData":[TD([[makeQuery(id+"F4.imprint","IMPRINT",EDGE,{"derivedFrom":sQuery(id+"F4.wireOp",EDGE,"E19")}),1.0]])]}),makeQuery(id+"F5.imprint","IMPRINT",FACE,{"disambiguationData":[TD([[makeQuery(id+"F5.imprint","IMPRINT",EDGE,{"derivedFrom":sQuery(id+"F5.wireOp",EDGE,"E24.0")}),-1.0]])]})])]}),"instanceName":"1"});
            var Q4;
            Q4=makeQuery(id+"F7.opPattern","COPY",BODY,{"derivedFrom":makeQuery(id+"F6.opLoft","SWEPT_BODY",BODY,{"disambiguationData":[OSD([makeQuery(id+"F4.imprint","IMPRINT",FACE,{"disambiguationData":[TD([[makeQuery(id+"F4.imprint","IMPRINT",EDGE,{"derivedFrom":sQuery(id+"F4.wireOp",EDGE,"E19")}),1.0]])]}),makeQuery(id+"F5.imprint","IMPRINT",FACE,{"disambiguationData":[TD([[makeQuery(id+"F5.imprint","IMPRINT",EDGE,{"derivedFrom":sQuery(id+"F5.wireOp",EDGE,"E24.0")}),-1.0]])]})])]}),"instanceName":"3"});
            var Q5;
            Q5=makeQuery(id+"F7.opPattern","COPY",BODY,{"derivedFrom":makeQuery(id+"F6.opLoft","SWEPT_BODY",BODY,{"disambiguationData":[OSD([makeQuery(id+"F4.imprint","IMPRINT",FACE,{"disambiguationData":[TD([[makeQuery(id+"F4.imprint","IMPRINT",EDGE,{"derivedFrom":sQuery(id+"F4.wireOp",EDGE,"E19")}),1.0]])]}),makeQuery(id+"F5.imprint","IMPRINT",FACE,{"disambiguationData":[TD([[makeQuery(id+"F5.imprint","IMPRINT",EDGE,{"derivedFrom":sQuery(id+"F5.wireOp",EDGE,"E24.0")}),-1.0]])]})])]}),"instanceName":"5"});
            var Q6;
            Q6=makeQuery(id+"F7.opPattern","COPY",BODY,{"derivedFrom":makeQuery(id+"F6.opLoft","SWEPT_BODY",BODY,{"disambiguationData":[OSD([makeQuery(id+"F4.imprint","IMPRINT",FACE,{"disambiguationData":[TD([[makeQuery(id+"F4.imprint","IMPRINT",EDGE,{"derivedFrom":sQuery(id+"F4.wireOp",EDGE,"E19")}),1.0]])]}),makeQuery(id+"F5.imprint","IMPRINT",FACE,{"disambiguationData":[TD([[makeQuery(id+"F5.imprint","IMPRINT",EDGE,{"derivedFrom":sQuery(id+"F5.wireOp",EDGE,"E24.0")}),-1.0]])]})])]}),"instanceName":"6"});
            var Q7;
            Q7=makeQuery(id+"F7.opPattern","COPY",BODY,{"derivedFrom":makeQuery(id+"F6.opLoft","SWEPT_BODY",BODY,{"disambiguationData":[OSD([makeQuery(id+"F4.imprint","IMPRINT",FACE,{"disambiguationData":[TD([[makeQuery(id+"F4.imprint","IMPRINT",EDGE,{"derivedFrom":sQuery(id+"F4.wireOp",EDGE,"E19")}),1.0]])]}),makeQuery(id+"F5.imprint","IMPRINT",FACE,{"disambiguationData":[TD([[makeQuery(id+"F5.imprint","IMPRINT",EDGE,{"derivedFrom":sQuery(id+"F5.wireOp",EDGE,"E24.0")}),-1.0]])]})])]}),"instanceName":"7"});
            var Q8;
            Q8=makeQuery(id+"F7.opPattern","COPY",BODY,{"derivedFrom":makeQuery(id+"F6.opLoft","SWEPT_BODY",BODY,{"disambiguationData":[OSD([makeQuery(id+"F4.imprint","IMPRINT",FACE,{"disambiguationData":[TD([[makeQuery(id+"F4.imprint","IMPRINT",EDGE,{"derivedFrom":sQuery(id+"F4.wireOp",EDGE,"E19")}),1.0]])]}),makeQuery(id+"F5.imprint","IMPRINT",FACE,{"disambiguationData":[TD([[makeQuery(id+"F5.imprint","IMPRINT",EDGE,{"derivedFrom":sQuery(id+"F5.wireOp",EDGE,"E24.0")}),-1.0]])]})])]}),"instanceName":"8"});
            var Q9;
            Q9=makeQuery(id+"F7.opPattern","COPY",BODY,{"derivedFrom":makeQuery(id+"F6.opLoft","SWEPT_BODY",BODY,{"disambiguationData":[OSD([makeQuery(id+"F4.imprint","IMPRINT",FACE,{"disambiguationData":[TD([[makeQuery(id+"F4.imprint","IMPRINT",EDGE,{"derivedFrom":sQuery(id+"F4.wireOp",EDGE,"E19")}),1.0]])]}),makeQuery(id+"F5.imprint","IMPRINT",FACE,{"disambiguationData":[TD([[makeQuery(id+"F5.imprint","IMPRINT",EDGE,{"derivedFrom":sQuery(id+"F5.wireOp",EDGE,"E24.0")}),-1.0]])]})])]}),"instanceName":"9"});
            var Q10;
            Q10=makeQuery(id+"F1.opRevolve","SWEPT_BODY",BODY,{"disambiguationData":[OSD([sQuery(id+"F0.wireOp",EDGE,"E1"),sQuery(id+"F0.wireOp",EDGE,"E2"),sQuery(id+"F0.wireOp",EDGE,"E3"),sQuery(id+"F0.wireOp",EDGE,"E4"),sQuery(id+"F0.wireOp",EDGE,"E5"),sQuery(id+"F0.wireOp",EDGE,"E6"),sQuery(id+"F0.wireOp",EDGE,"E7"),sQuery(id+"F0.wireOp",EDGE,"E8"),sQuery(id+"F0.wireOp",EDGE,"E9"),sQuery(id+"F0.wireOp",EDGE,"E10")])]});
            booleanBodies(context, id + "F8", {"operationType" : BooleanOperationType.SUBTRACTION, "tools" : qUnion([Q0, Q1, Q2, Q3, Q4, Q5, Q6, Q7, Q8, Q9]), "targets" : qUnion([Q10])});
        }
        {
            var Q0;
            Q0=qCreatedBy(makeId("Front.planeOp"),FACE);
            var sketch = newSketch(context, id + "F9", { "sketchPlane" : qUnion([Q0])});
            skLineSegment(sketch, "E30", {"start": v(0, 0) * mm, "end": v(0, 20) * mm, "construction": true});
            skSolve(sketch);
        }
        {
            var Q0;
            Q0=makeQuery(id+"F1.opRevolve","SWEPT_BODY",BODY,{"disambiguationData":[OSD([sQuery(id+"F0.wireOp",EDGE,"E1"),sQuery(id+"F0.wireOp",EDGE,"E2"),sQuery(id+"F0.wireOp",EDGE,"E3"),sQuery(id+"F0.wireOp",EDGE,"E4"),sQuery(id+"F0.wireOp",EDGE,"E5"),sQuery(id+"F0.wireOp",EDGE,"E6"),sQuery(id+"F0.wireOp",EDGE,"E7"),sQuery(id+"F0.wireOp",EDGE,"E8"),sQuery(id+"F0.wireOp",EDGE,"E9"),sQuery(id+"F0.wireOp",EDGE,"E10")])]});
            var Q1;
            Q1=sQuery(id+"F9.wireOp",EDGE,"E30");
            circularPattern(context, id + "F10", {"entities" : qUnion([Q0]), "axis" : qUnion([Q1]), "angle" : 180 * degree, "instanceCount" : 3, "equalSpace" : true});
        }
        {
            var Q0;
            Q0=makeQuery(id+"F1.opRevolve","SWEPT_BODY",BODY,{"disambiguationData":[OSD([sQuery(id+"F0.wireOp",EDGE,"E1"),sQuery(id+"F0.wireOp",EDGE,"E2"),sQuery(id+"F0.wireOp",EDGE,"E3"),sQuery(id+"F0.wireOp",EDGE,"E4"),sQuery(id+"F0.wireOp",EDGE,"E5"),sQuery(id+"F0.wireOp",EDGE,"E6"),sQuery(id+"F0.wireOp",EDGE,"E7"),sQuery(id+"F0.wireOp",EDGE,"E8"),sQuery(id+"F0.wireOp",EDGE,"E9"),sQuery(id+"F0.wireOp",EDGE,"E10")])]});
            deleteBodies(context, id + "F11", {"entities" : qUnion([Q0])});
        }
        {
            var Q0;
            Q0=makeQuery(id+"F10.opPattern","COPY",BODY,{"derivedFrom":makeQuery(id+"F1.opRevolve","SWEPT_BODY",BODY,{"disambiguationData":[OSD([sQuery(id+"F0.wireOp",EDGE,"E1"),sQuery(id+"F0.wireOp",EDGE,"E2"),sQuery(id+"F0.wireOp",EDGE,"E3"),sQuery(id+"F0.wireOp",EDGE,"E4"),sQuery(id+"F0.wireOp",EDGE,"E5"),sQuery(id+"F0.wireOp",EDGE,"E6"),sQuery(id+"F0.wireOp",EDGE,"E7"),sQuery(id+"F0.wireOp",EDGE,"E8"),sQuery(id+"F0.wireOp",EDGE,"E9"),sQuery(id+"F0.wireOp",EDGE,"E10")])]}),"instanceName":"1"});
            var Q1;
            Q1=makeQuery(id+"F10.opPattern","COPY",EDGE,{"derivedFrom":makeQuery(id+"F1.opRevolve","SWEPT_EDGE",EDGE,{"disambiguationData":[OSD([sQuery(id+"F0.wireOp",EDGE,"E2"),sQuery(id+"F0.wireOp",EDGE,"E3")])]}),"instanceName":"1"});
            transform(context, id + "F12", {"entities" : qUnion([Q0]), "transformType" : TransformType.ROTATION, "transformAxis" : qUnion([Q1]), "angle" : 18 * degree, "makeCopy" : false});
        }
        {
            var Q0;
            Q0=makeQuery(id+"F10.opPattern","COPY",FACE,{"derivedFrom":makeQuery(id+"F1.opRevolve","SWEPT_FACE",FACE,{"disambiguationData":[OSD([sQuery(id+"F0.wireOp",EDGE,"E3")])]}),"instanceName":"1"});
            var sketch = newSketch(context, id + "F13", { "sketchPlane" : qUnion([Q0])});
            skCircle(sketch, "E31", {"center": v(0, 0) * mm, "radius": 5 * mm});
            skCircle(sketch, "E32", {"center": v(0, 0) * mm, "radius": 2 * mm});
            skLineSegment(sketch, "E33.bottom", {"start": v(5, 0) * mm, "end": v(-5, 0) * mm});
            skLineSegment(sketch, "E33.top", {"start": v(5, -20) * mm, "end": v(-5, -20) * mm});
            skLineSegment(sketch, "E33.left", {"start": v(5, 0) * mm, "end": v(5, -20) * mm});
            skLineSegment(sketch, "E33.right", {"start": v(-5, 0) * mm, "end": v(-5, -20) * mm});
            skPoint(sketch, "E33.middle", {"position": v(0, -10) * mm});
            skSolve(sketch);
        }
        {
            var Q0;
            Q0 = qSketchRegion(id + "F13", true);
            extrude(context, id + "F14", {"entities" : qUnion([Q0]), "depth" : 5 * mm, "offsetDistance" : 25 * mm});
        }
        {
            var Q0;
            Q0=makeQuery(id+"F14.opExtrude","SWEPT_BODY",BODY,{"disambiguationData":[OSD([sQuery(id+"F13.wireOp",EDGE,"E31"),sQuery(id+"F13.wireOp",EDGE,"E32"),sQuery(id+"F13.wireOp",EDGE,"E33.top"),sQuery(id+"F13.wireOp",EDGE,"E33.left"),sQuery(id+"F13.wireOp",EDGE,"E33.right")])]});
            var Q1;
            Q1=sQuery(id+"F9.wireOp",EDGE,"E30");
            circularPattern(context, id + "F15", {"entities" : qUnion([Q0]), "axis" : qUnion([Q1]), "angle" : 90 * degree, "instanceCount" : 2, "equalSpace" : true});
        }
        {
            var Q0;
            Q0=makeQuery(id+"F14.opExtrude","SWEPT_FACE",FACE,{"disambiguationData":[OSD([sQuery(id+"F13.wireOp",EDGE,"E33.top")])]});
            var sketch = newSketch(context, id + "F16", { "sketchPlane" : qUnion([Q0])});
            skPoint(sketch, "E34.middle", {"position": v(0, 0) * mm});
            skLineSegment(sketch, "E35.bottom", {"start": v(10, 10) * mm, "end": v(-33, 10) * mm});
            skLineSegment(sketch, "E35.top", {"start": v(10, -33) * mm, "end": v(-33, -33) * mm});
            skLineSegment(sketch, "E35.left", {"start": v(10, 10) * mm, "end": v(10, -33) * mm});
            skLineSegment(sketch, "E35.right", {"start": v(-33, 10) * mm, "end": v(-33, -33) * mm});
            skPoint(sketch, "E35.middle", {"position": v(-11.5, -11.5) * mm});
            skSolve(sketch);
        }
        {
            var Q0;
            Q0 = qSketchRegion(id + "F16", true);
            extrude(context, id + "F17", {"entities" : qUnion([Q0]), "operationType" : NewBodyOperationType.ADD, "depth" : 2 * mm, "offsetDistance" : 25 * mm});
        }
    });
